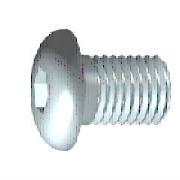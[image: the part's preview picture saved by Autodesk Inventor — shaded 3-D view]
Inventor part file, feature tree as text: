
AUTODESK INVENTOR PART (.ipt)
format: ipt  version: 2022 (Build 260153000, 153)  size: 215,040 bytes
history: native  units: mm (DEFAULTED — no unit token found)
features: sketch x2, extrude x1, plane x1, fillet x1
ambient origin geometry x7: Origin, YZ Plane, XY Plane, X Axis, Y Axis, Z Axis, Center Point
bodies: Solid1 (feature_tree), Body (feature_tree)
feature tree (5):
  extrude  "Slot"  Depth=1.65mm
  plane  "Work Plane1"
  fillet  "Fillet2"  Radius=1.65mm
  sketch  "Sketch1"  dims[d1=5.0mm d2=0.306825mm d3=1.65mm]
  sketch  "Sketch2"  dims[d4=1.04mm d5=60.0deg d6=3.0mm d7=3.0mm d8=2.309401mm d9=5.7mm d10=90.0deg d11=10.0mm d12=0.0mm d13=5.0mm d14=0.0mm d15=0.306725mm d16=0.306725mm d17=1.45mm d19=0.0mm d26=6.0mm d27=45.0deg d28=0.0mm d29=0.0mm d30=0.1mm]
